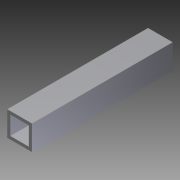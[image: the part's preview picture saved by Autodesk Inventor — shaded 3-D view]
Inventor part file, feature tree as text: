
AUTODESK INVENTOR PART (.ipt)
format: ipt  version: 2012 (Build 160160000, 160)  size: 77,312 bytes
history: native  units: in
note: dims shown in document units (in); Inventor stores cm internally (conversion verified against a paired STEP export)
features: extrude x1, sketch x1
ambient origin geometry x8: Origin, YZ Plane, XZ Plane, XY Plane, X Axis, Y Axis, Z Axis, Center Point
bodies: Solid1 (feature_tree)
feature tree (2):
  extrude  "Extrusion1"  Depth=0.125in
  sketch  "Sketch1"  dims[d0=0.125in d1=0.125in d2=0.125in d3=0.125in d4=1.0in d5=1.0in d6=5.702in d7=0.0in]
